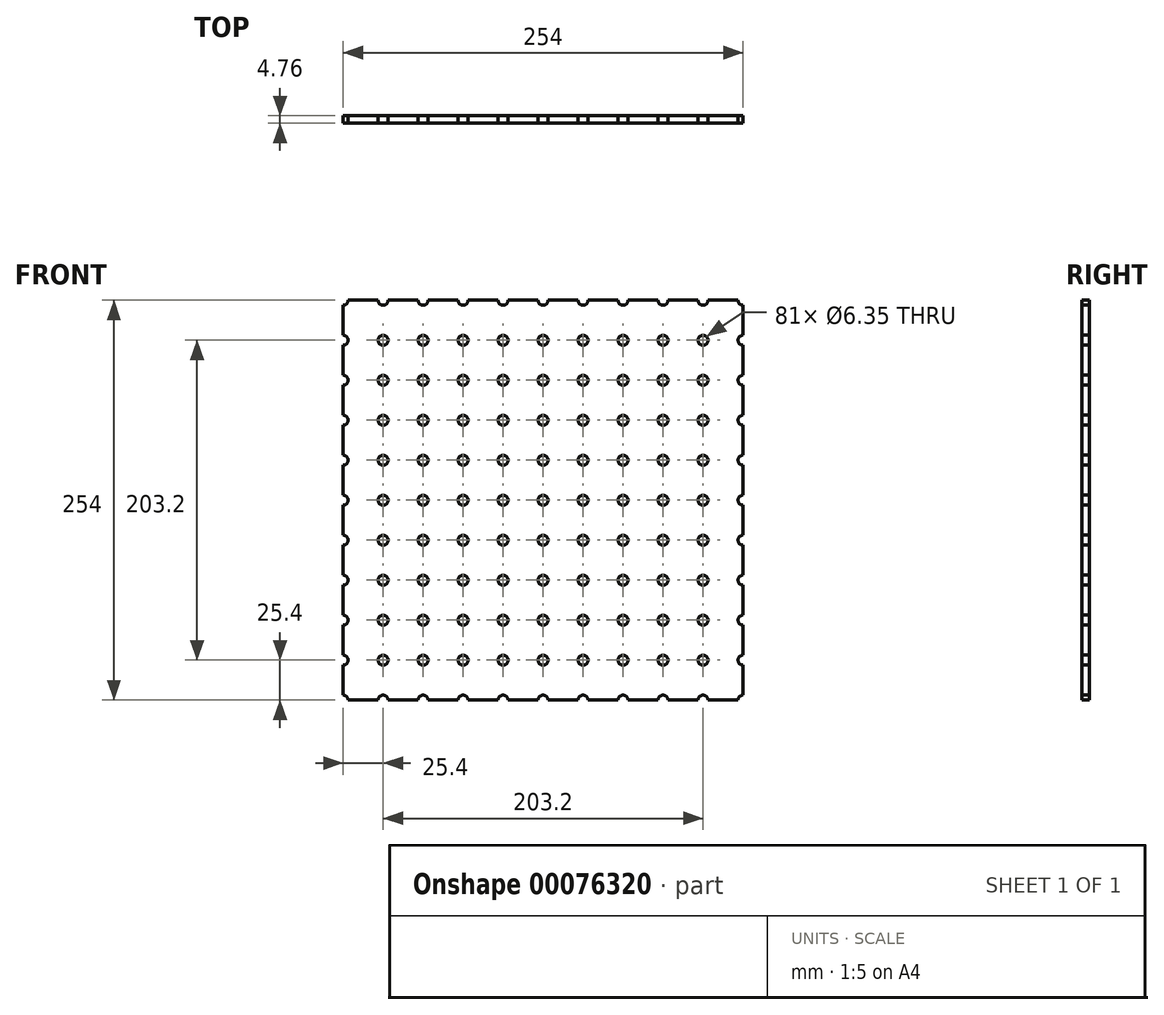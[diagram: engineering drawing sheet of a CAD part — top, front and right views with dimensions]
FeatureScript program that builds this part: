
annotation { "Feature Type Name" : "Feature", "Feature Type Description" : "" }
export const myFeature = defineFeature(function(context is Context, id is Id, definition is map)
    precondition{}
    {
        {
            var Q0;
            Q0=qCreatedBy(makeId("Front.planeOp"),FACE);
            var sketch = newSketch(context, id + "F0", { "sketchPlane" : qUnion([Q0])});
            skLineSegment(sketch, "E0.bottom", {"start": v(-127, 127) * mm, "end": v(127, 127) * mm});
            skLineSegment(sketch, "E0.top", {"start": v(-127, -127) * mm, "end": v(127, -127) * mm});
            skLineSegment(sketch, "E0.left", {"start": v(-127, 127) * mm, "end": v(-127, -127) * mm});
            skLineSegment(sketch, "E0.right", {"start": v(127, 127) * mm, "end": v(127, -127) * mm});
            skPoint(sketch, "E0.middle", {"position": v(0, 0) * mm});
            skCircle(sketch, "E1", {"center": v(-101.6, 101.6) * mm, "radius": 3.18 * mm});
            skCircle(sketch, "E2", {"center": v(-127, 127) * mm, "radius": 3.18 * mm});
            skCircle(sketch, "E3", {"center": v(-101.6, 127) * mm, "radius": 3.18 * mm});
            skCircle(sketch, "E4", {"center": v(-127, 101.6) * mm, "radius": 3.18 * mm});
            skCircle(sketch, "E5.0.1.0", {"center": v(-127, 50.8) * mm, "radius": 3.18 * mm});
            skCircle(sketch, "E5.0.1.1", {"center": v(-101.6, 50.8) * mm, "radius": 3.18 * mm});
            skCircle(sketch, "E5.0.1.2", {"center": v(-101.6, 76.2) * mm, "radius": 3.18 * mm});
            skCircle(sketch, "E5.0.1.3", {"center": v(-127, 76.2) * mm, "radius": 3.18 * mm});
            skCircle(sketch, "E5.0.2.0", {"center": v(-127, 0) * mm, "radius": 3.18 * mm});
            skCircle(sketch, "E5.0.2.1", {"center": v(-101.6, 0) * mm, "radius": 3.18 * mm});
            skCircle(sketch, "E5.0.2.2", {"center": v(-101.6, 25.4) * mm, "radius": 3.18 * mm});
            skCircle(sketch, "E5.0.2.3", {"center": v(-127, 25.4) * mm, "radius": 3.18 * mm});
            skCircle(sketch, "E5.0.3.0", {"center": v(-127, -50.8) * mm, "radius": 3.18 * mm});
            skCircle(sketch, "E5.0.3.1", {"center": v(-101.6, -50.8) * mm, "radius": 3.18 * mm});
            skCircle(sketch, "E5.0.3.2", {"center": v(-101.6, -25.4) * mm, "radius": 3.18 * mm});
            skCircle(sketch, "E5.0.3.3", {"center": v(-127, -25.4) * mm, "radius": 3.18 * mm});
            skCircle(sketch, "E5.0.4.0", {"center": v(-127, -101.6) * mm, "radius": 3.18 * mm});
            skCircle(sketch, "E5.0.4.1", {"center": v(-101.6, -101.6) * mm, "radius": 3.18 * mm});
            skCircle(sketch, "E5.0.4.2", {"center": v(-101.6, -76.2) * mm, "radius": 3.18 * mm});
            skCircle(sketch, "E5.0.4.3", {"center": v(-127, -76.2) * mm, "radius": 3.18 * mm});
            skCircle(sketch, "E5.0.5.2", {"center": v(-101.6, -127) * mm, "radius": 3.18 * mm});
            skCircle(sketch, "E5.0.5.3", {"center": v(-127, -127) * mm, "radius": 3.18 * mm});
            skCircle(sketch, "E5.1.0.0", {"center": v(-76.2, 101.6) * mm, "radius": 3.18 * mm});
            skCircle(sketch, "E5.1.0.1", {"center": v(-50.8, 101.6) * mm, "radius": 3.18 * mm});
            skCircle(sketch, "E5.1.0.2", {"center": v(-50.8, 127) * mm, "radius": 3.18 * mm});
            skCircle(sketch, "E5.1.0.3", {"center": v(-76.2, 127) * mm, "radius": 3.18 * mm});
            skCircle(sketch, "E5.1.1.0", {"center": v(-76.2, 50.8) * mm, "radius": 3.18 * mm});
            skCircle(sketch, "E5.1.1.1", {"center": v(-50.8, 50.8) * mm, "radius": 3.18 * mm});
            skCircle(sketch, "E5.1.1.2", {"center": v(-50.8, 76.2) * mm, "radius": 3.18 * mm});
            skCircle(sketch, "E5.1.1.3", {"center": v(-76.2, 76.2) * mm, "radius": 3.18 * mm});
            skCircle(sketch, "E5.1.2.0", {"center": v(-76.2, 0) * mm, "radius": 3.18 * mm});
            skCircle(sketch, "E5.1.2.1", {"center": v(-50.8, 0) * mm, "radius": 3.18 * mm});
            skCircle(sketch, "E5.1.2.2", {"center": v(-50.8, 25.4) * mm, "radius": 3.18 * mm});
            skCircle(sketch, "E5.1.2.3", {"center": v(-76.2, 25.4) * mm, "radius": 3.18 * mm});
            skCircle(sketch, "E5.1.3.0", {"center": v(-76.2, -50.8) * mm, "radius": 3.18 * mm});
            skCircle(sketch, "E5.1.3.1", {"center": v(-50.8, -50.8) * mm, "radius": 3.18 * mm});
            skCircle(sketch, "E5.1.3.2", {"center": v(-50.8, -25.4) * mm, "radius": 3.18 * mm});
            skCircle(sketch, "E5.1.3.3", {"center": v(-76.2, -25.4) * mm, "radius": 3.18 * mm});
            skCircle(sketch, "E5.1.4.0", {"center": v(-76.2, -101.6) * mm, "radius": 3.18 * mm});
            skCircle(sketch, "E5.1.4.1", {"center": v(-50.8, -101.6) * mm, "radius": 3.18 * mm});
            skCircle(sketch, "E5.1.4.2", {"center": v(-50.8, -76.2) * mm, "radius": 3.18 * mm});
            skCircle(sketch, "E5.1.4.3", {"center": v(-76.2, -76.2) * mm, "radius": 3.18 * mm});
            skCircle(sketch, "E5.1.5.2", {"center": v(-50.8, -127) * mm, "radius": 3.18 * mm});
            skCircle(sketch, "E5.1.5.3", {"center": v(-76.2, -127) * mm, "radius": 3.18 * mm});
            skCircle(sketch, "E5.2.0.0", {"center": v(-25.4, 101.6) * mm, "radius": 3.18 * mm});
            skCircle(sketch, "E5.2.0.1", {"center": v(0, 101.6) * mm, "radius": 3.18 * mm});
            skCircle(sketch, "E5.2.0.2", {"center": v(0, 127) * mm, "radius": 3.18 * mm});
            skCircle(sketch, "E5.2.0.3", {"center": v(-25.4, 127) * mm, "radius": 3.18 * mm});
            skCircle(sketch, "E5.2.1.0", {"center": v(-25.4, 50.8) * mm, "radius": 3.18 * mm});
            skCircle(sketch, "E5.2.1.1", {"center": v(0, 50.8) * mm, "radius": 3.18 * mm});
            skCircle(sketch, "E5.2.1.2", {"center": v(0, 76.2) * mm, "radius": 3.18 * mm});
            skCircle(sketch, "E5.2.1.3", {"center": v(-25.4, 76.2) * mm, "radius": 3.18 * mm});
            skCircle(sketch, "E5.2.2.0", {"center": v(-25.4, 0) * mm, "radius": 3.18 * mm});
            skCircle(sketch, "E5.2.2.1", {"center": v(0, 0) * mm, "radius": 3.18 * mm});
            skCircle(sketch, "E5.2.2.2", {"center": v(0, 25.4) * mm, "radius": 3.18 * mm});
            skCircle(sketch, "E5.2.2.3", {"center": v(-25.4, 25.4) * mm, "radius": 3.18 * mm});
            skCircle(sketch, "E5.2.3.0", {"center": v(-25.4, -50.8) * mm, "radius": 3.18 * mm});
            skCircle(sketch, "E5.2.3.1", {"center": v(0, -50.8) * mm, "radius": 3.18 * mm});
            skCircle(sketch, "E5.2.3.2", {"center": v(0, -25.4) * mm, "radius": 3.18 * mm});
            skCircle(sketch, "E5.2.3.3", {"center": v(-25.4, -25.4) * mm, "radius": 3.18 * mm});
            skCircle(sketch, "E5.2.4.0", {"center": v(-25.4, -101.6) * mm, "radius": 3.18 * mm});
            skCircle(sketch, "E5.2.4.1", {"center": v(0, -101.6) * mm, "radius": 3.18 * mm});
            skCircle(sketch, "E5.2.4.2", {"center": v(0, -76.2) * mm, "radius": 3.18 * mm});
            skCircle(sketch, "E5.2.4.3", {"center": v(-25.4, -76.2) * mm, "radius": 3.18 * mm});
            skCircle(sketch, "E5.2.5.2", {"center": v(0, -127) * mm, "radius": 3.18 * mm});
            skCircle(sketch, "E5.2.5.3", {"center": v(-25.4, -127) * mm, "radius": 3.18 * mm});
            skCircle(sketch, "E5.3.0.0", {"center": v(25.4, 101.6) * mm, "radius": 3.18 * mm});
            skCircle(sketch, "E5.3.0.1", {"center": v(50.8, 101.6) * mm, "radius": 3.18 * mm});
            skCircle(sketch, "E5.3.0.2", {"center": v(50.8, 127) * mm, "radius": 3.18 * mm});
            skCircle(sketch, "E5.3.0.3", {"center": v(25.4, 127) * mm, "radius": 3.18 * mm});
            skCircle(sketch, "E5.3.1.0", {"center": v(25.4, 50.8) * mm, "radius": 3.18 * mm});
            skCircle(sketch, "E5.3.1.1", {"center": v(50.8, 50.8) * mm, "radius": 3.18 * mm});
            skCircle(sketch, "E5.3.1.2", {"center": v(50.8, 76.2) * mm, "radius": 3.18 * mm});
            skCircle(sketch, "E5.3.1.3", {"center": v(25.4, 76.2) * mm, "radius": 3.18 * mm});
            skCircle(sketch, "E5.3.2.0", {"center": v(25.4, 0) * mm, "radius": 3.18 * mm});
            skCircle(sketch, "E5.3.2.1", {"center": v(50.8, 0) * mm, "radius": 3.18 * mm});
            skCircle(sketch, "E5.3.2.2", {"center": v(50.8, 25.4) * mm, "radius": 3.18 * mm});
            skCircle(sketch, "E5.3.2.3", {"center": v(25.4, 25.4) * mm, "radius": 3.18 * mm});
            skCircle(sketch, "E5.3.3.0", {"center": v(25.4, -50.8) * mm, "radius": 3.18 * mm});
            skCircle(sketch, "E5.3.3.1", {"center": v(50.8, -50.8) * mm, "radius": 3.18 * mm});
            skCircle(sketch, "E5.3.3.2", {"center": v(50.8, -25.4) * mm, "radius": 3.18 * mm});
            skCircle(sketch, "E5.3.3.3", {"center": v(25.4, -25.4) * mm, "radius": 3.18 * mm});
            skCircle(sketch, "E5.3.4.0", {"center": v(25.4, -101.6) * mm, "radius": 3.18 * mm});
            skCircle(sketch, "E5.3.4.1", {"center": v(50.8, -101.6) * mm, "radius": 3.18 * mm});
            skCircle(sketch, "E5.3.4.2", {"center": v(50.8, -76.2) * mm, "radius": 3.18 * mm});
            skCircle(sketch, "E5.3.4.3", {"center": v(25.4, -76.2) * mm, "radius": 3.18 * mm});
            skCircle(sketch, "E5.3.5.2", {"center": v(50.8, -127) * mm, "radius": 3.18 * mm});
            skCircle(sketch, "E5.3.5.3", {"center": v(25.4, -127) * mm, "radius": 3.18 * mm});
            skCircle(sketch, "E5.4.0.0", {"center": v(76.2, 101.6) * mm, "radius": 3.18 * mm});
            skCircle(sketch, "E5.4.0.1", {"center": v(101.6, 101.6) * mm, "radius": 3.18 * mm});
            skCircle(sketch, "E5.4.0.2", {"center": v(101.6, 127) * mm, "radius": 3.18 * mm});
            skCircle(sketch, "E5.4.0.3", {"center": v(76.2, 127) * mm, "radius": 3.18 * mm});
            skCircle(sketch, "E5.4.1.0", {"center": v(76.2, 50.8) * mm, "radius": 3.18 * mm});
            skCircle(sketch, "E5.4.1.1", {"center": v(101.6, 50.8) * mm, "radius": 3.18 * mm});
            skCircle(sketch, "E5.4.1.2", {"center": v(101.6, 76.2) * mm, "radius": 3.18 * mm});
            skCircle(sketch, "E5.4.1.3", {"center": v(76.2, 76.2) * mm, "radius": 3.18 * mm});
            skCircle(sketch, "E5.4.2.0", {"center": v(76.2, 0) * mm, "radius": 3.18 * mm});
            skCircle(sketch, "E5.4.2.1", {"center": v(101.6, 0) * mm, "radius": 3.18 * mm});
            skCircle(sketch, "E5.4.2.2", {"center": v(101.6, 25.4) * mm, "radius": 3.18 * mm});
            skCircle(sketch, "E5.4.2.3", {"center": v(76.2, 25.4) * mm, "radius": 3.18 * mm});
            skCircle(sketch, "E5.4.3.0", {"center": v(76.2, -50.8) * mm, "radius": 3.18 * mm});
            skCircle(sketch, "E5.4.3.1", {"center": v(101.6, -50.8) * mm, "radius": 3.18 * mm});
            skCircle(sketch, "E5.4.3.2", {"center": v(101.6, -25.4) * mm, "radius": 3.18 * mm});
            skCircle(sketch, "E5.4.3.3", {"center": v(76.2, -25.4) * mm, "radius": 3.18 * mm});
            skCircle(sketch, "E5.4.4.0", {"center": v(76.2, -101.6) * mm, "radius": 3.18 * mm});
            skCircle(sketch, "E5.4.4.1", {"center": v(101.6, -101.6) * mm, "radius": 3.18 * mm});
            skCircle(sketch, "E5.4.4.2", {"center": v(101.6, -76.2) * mm, "radius": 3.18 * mm});
            skCircle(sketch, "E5.4.4.3", {"center": v(76.2, -76.2) * mm, "radius": 3.18 * mm});
            skCircle(sketch, "E5.4.5.2", {"center": v(101.6, -127) * mm, "radius": 3.18 * mm});
            skCircle(sketch, "E5.4.5.3", {"center": v(76.2, -127) * mm, "radius": 3.18 * mm});
            skCircle(sketch, "E5.5.0.0", {"center": v(127, 101.6) * mm, "radius": 3.18 * mm});
            skCircle(sketch, "E5.5.0.3", {"center": v(127, 127) * mm, "radius": 3.18 * mm});
            skCircle(sketch, "E5.5.1.0", {"center": v(127, 50.8) * mm, "radius": 3.18 * mm});
            skCircle(sketch, "E5.5.1.3", {"center": v(127, 76.2) * mm, "radius": 3.18 * mm});
            skCircle(sketch, "E5.5.2.0", {"center": v(127, 0) * mm, "radius": 3.18 * mm});
            skCircle(sketch, "E5.5.2.3", {"center": v(127, 25.4) * mm, "radius": 3.18 * mm});
            skCircle(sketch, "E5.5.3.0", {"center": v(127, -50.8) * mm, "radius": 3.18 * mm});
            skCircle(sketch, "E5.5.3.3", {"center": v(127, -25.4) * mm, "radius": 3.18 * mm});
            skCircle(sketch, "E5.5.4.0", {"center": v(127, -101.6) * mm, "radius": 3.18 * mm});
            skCircle(sketch, "E5.5.4.3", {"center": v(127, -76.2) * mm, "radius": 3.18 * mm});
            skCircle(sketch, "E5.5.5.3", {"center": v(127, -127) * mm, "radius": 3.18 * mm});
            skLineSegment(sketch, "E5.direction1", {"start": v(-127, 101.6) * mm, "end": v(-76.2, 101.6) * mm, "construction": true});
            skLineSegment(sketch, "E5.direction2", {"start": v(-127, 101.6) * mm, "end": v(-127, 50.8) * mm, "construction": true});
            skSolve(sketch);
        }
        {
            var Q0;
            Q0=makeQuery(id+"F0.imprint","IMPRINT",FACE,{"disambiguationData":[TD([[makeQuery(id+"F0.imprint","IMPRINT",EDGE,{"derivedFrom":sQuery(id+"F0.wireOp",EDGE,"E1")}),-1.0]])]});
            extrude(context, id + "F1", {"entities" : qUnion([Q0]), "endBound" : BoundingType.SYMMETRIC, "depth" : 4.76 * mm});
        }
    });
